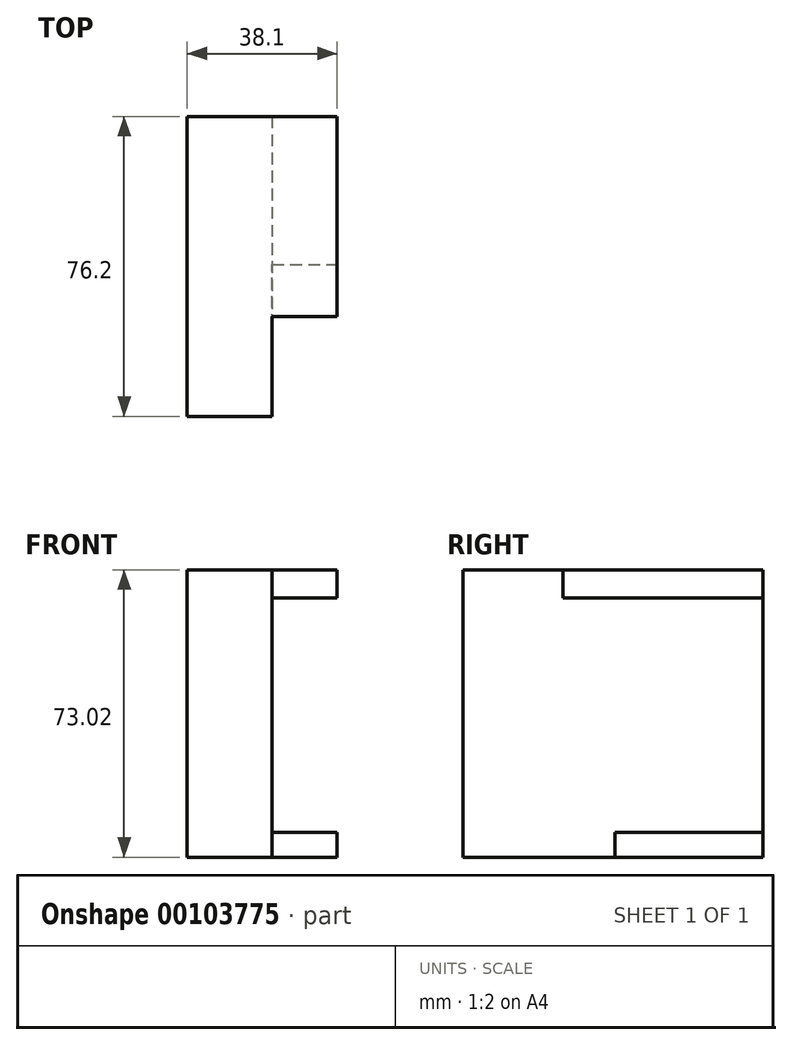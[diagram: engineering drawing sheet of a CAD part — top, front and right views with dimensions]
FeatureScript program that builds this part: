
annotation { "Feature Type Name" : "Feature", "Feature Type Description" : "" }
export const myFeature = defineFeature(function(context is Context, id is Id, definition is map)
    precondition{}
    {
        {
            var Q0;
            Q0=qCreatedBy(makeId("Front.planeOp"),FACE);
            var sketch = newSketch(context, id + "F0", { "sketchPlane" : qUnion([Q0])});
            skLineSegment(sketch, "E0.bottom", {"start": v(19.05, 34.26) * mm, "end": v(-19.05, 34.26) * mm});
            skLineSegment(sketch, "E0.top", {"start": v(19.05, -38.76) * mm, "end": v(-19.05, -38.76) * mm});
            skLineSegment(sketch, "E0.left", {"start": v(19.05, 34.26) * mm, "end": v(19.05, -38.76) * mm});
            skLineSegment(sketch, "E0.right", {"start": v(-19.05, 34.26) * mm, "end": v(-19.05, -38.76) * mm});
            skPoint(sketch, "E0.middle", {"position": v(0, -2.25) * mm});
            skSolve(sketch);
        }
        {
            var Q0;
            Q0=makeQuery(id+"F0.imprint","IMPRINT",FACE,{"disambiguationData":[TD([[makeQuery(id+"F0.imprint","IMPRINT",EDGE,{"derivedFrom":sQuery(id+"F0.wireOp",EDGE,"E0.bottom")}),1.0]])]});
            extrude(context, id + "F1", {"entities" : qUnion([Q0]), "depth" : 76.2 * mm});
        }
        {
            var Q0;
            Q0=makeQuery(id+"F1.opExtrude","SWEPT_FACE",FACE,{"disambiguationData":[OSD([sQuery(id+"F0.wireOp",EDGE,"E0.left")])]});
            var sketch = newSketch(context, id + "F2", { "sketchPlane" : qUnion([Q0])});
            skLineSegment(sketch, "E1.bottom", {"start": v(0, 34.26) * mm, "end": v(-50.8, 34.26) * mm});
            skLineSegment(sketch, "E1.top", {"start": v(0, 27.12) * mm, "end": v(-50.8, 27.12) * mm});
            skLineSegment(sketch, "E1.left", {"start": v(0, 34.26) * mm, "end": v(0, 27.12) * mm});
            skLineSegment(sketch, "E1.right", {"start": v(-50.8, 34.26) * mm, "end": v(-50.8, 27.12) * mm});
            skLineSegment(sketch, "E2.bottom", {"start": v(0, -38.76) * mm, "end": v(-37.64, -38.76) * mm});
            skLineSegment(sketch, "E2.top", {"start": v(0, -32.46) * mm, "end": v(-37.64, -32.46) * mm});
            skLineSegment(sketch, "E2.left", {"start": v(0, -38.76) * mm, "end": v(0, -32.46) * mm});
            skLineSegment(sketch, "E2.right", {"start": v(-37.64, -38.76) * mm, "end": v(-37.64, -32.46) * mm});
            skSolve(sketch);
        }
        {
            var Q0;
            {var subQ5=sQuery(id+"F2.wireOp",EDGE,"E1.top");Q0=makeQuery(id+"F2.imprint","IMPRINT",FACE,{"disambiguationData":[TD([[makeQuery(id+"F2.imprint","IMPRINT",EDGE,{"derivedFrom":subQ5}),1.0]])]});}
            extrude(context, id + "F3", {"entities" : qUnion([Q0]), "operationType" : NewBodyOperationType.REMOVE, "oppositeDirection" : true, "depth" : 16.5 * mm});
        }
    });
